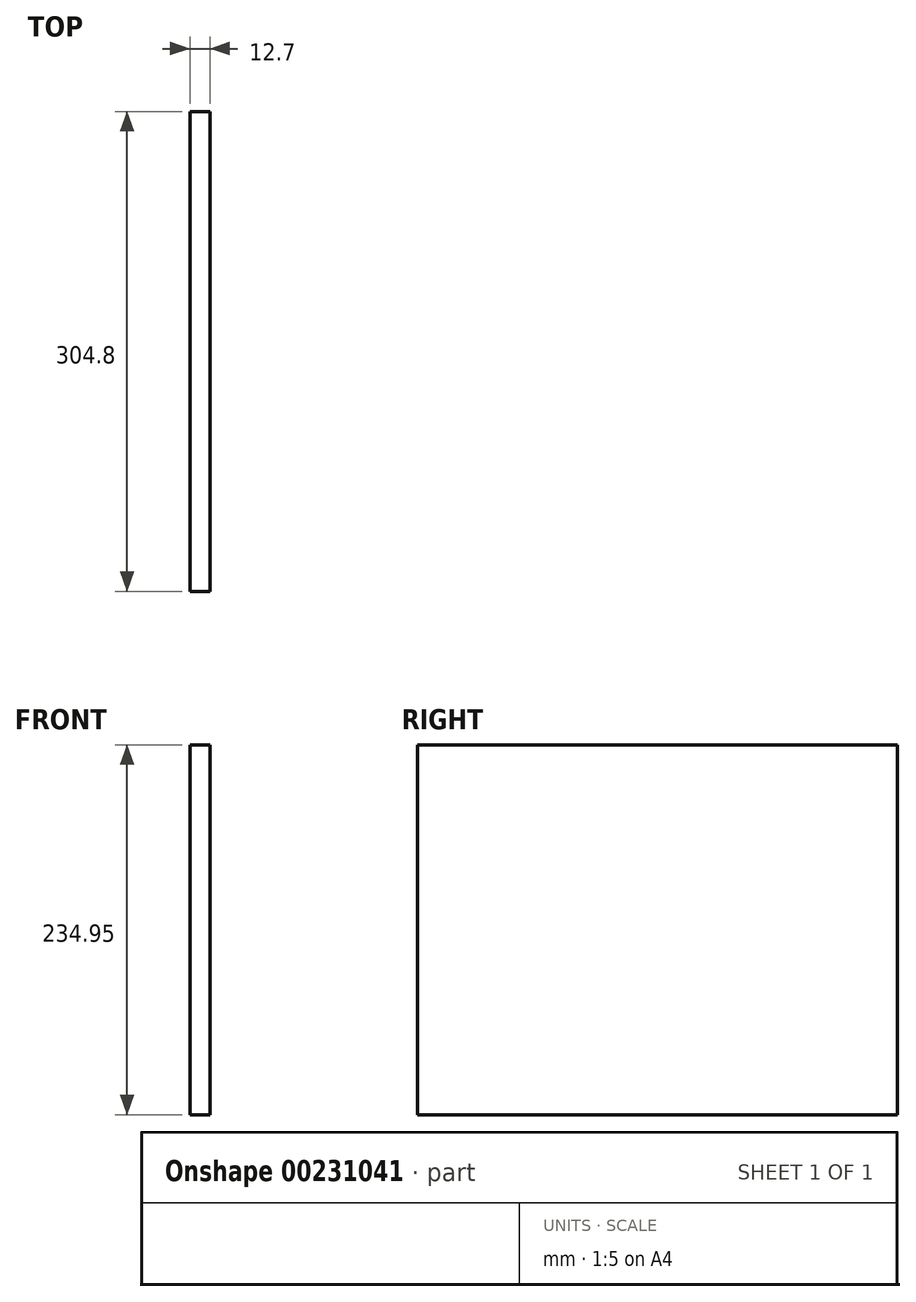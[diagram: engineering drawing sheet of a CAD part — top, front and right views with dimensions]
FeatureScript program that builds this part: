
annotation { "Feature Type Name" : "Feature", "Feature Type Description" : "" }
export const myFeature = defineFeature(function(context is Context, id is Id, definition is map)
    precondition{}
    {
        {
            var Q0;
            Q0=qCreatedBy(makeId("Right.planeOp"),FACE);
            var sketch = newSketch(context, id + "F0", { "sketchPlane" : qUnion([Q0])});
            skLineSegment(sketch, "E0.bottom", {"start": v(-152.4, 234.95) * mm, "end": v(152.4, 234.95) * mm});
            skLineSegment(sketch, "E0.top", {"start": v(-152.4, 0) * mm, "end": v(152.4, 0) * mm});
            skLineSegment(sketch, "E0.left", {"start": v(-152.4, 234.95) * mm, "end": v(-152.4, 0) * mm});
            skLineSegment(sketch, "E0.right", {"start": v(152.4, 234.95) * mm, "end": v(152.4, 0) * mm});
            skSolve(sketch);
        }
        {
            var Q0;
            Q0 = qSketchRegion(id + "F0", true);
            extrude(context, id + "F1", {"entities" : qUnion([Q0]), "depth" : 12.7 * mm});
        }
    });
